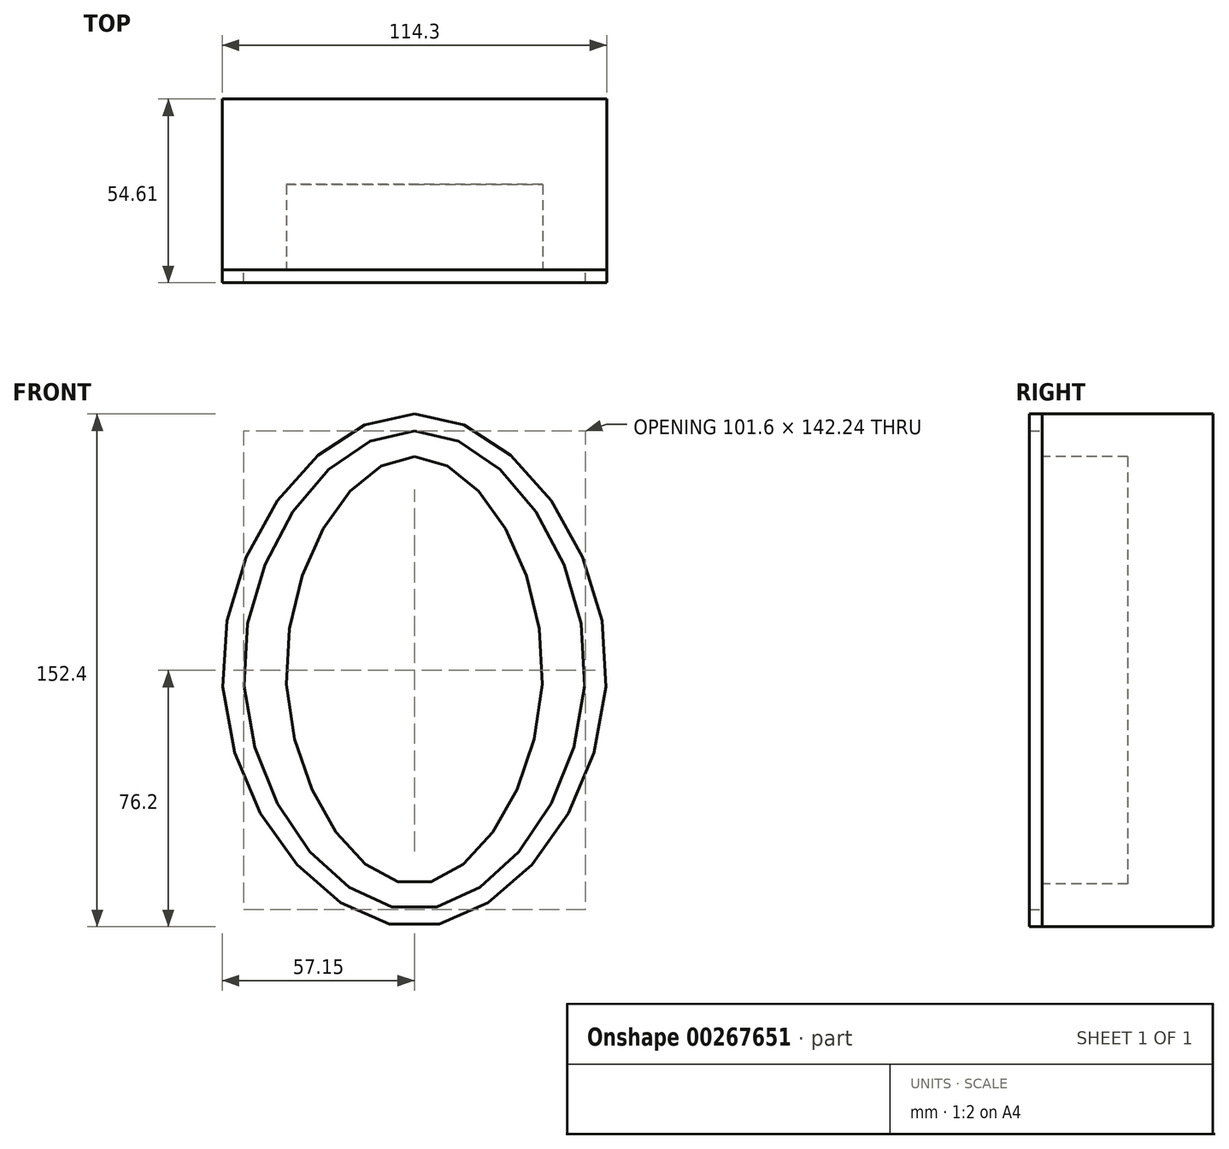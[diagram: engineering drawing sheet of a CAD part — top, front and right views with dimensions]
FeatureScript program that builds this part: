
annotation { "Feature Type Name" : "Feature", "Feature Type Description" : "" }
export const myFeature = defineFeature(function(context is Context, id is Id, definition is map)
    precondition{}
    {
        {
            var Q0;
            Q0=qCreatedBy(makeId("Front.planeOp"),FACE);
            var sketch = newSketch(context, id + "F0", { "sketchPlane" : qUnion([Q0])});
            skFitSpline(sketch, "E0", {"points": [v(0, 76.2) * mm, v(57.15, 0) * mm, v(0, -76.2) * mm, v(-57.15, 0) * mm, v(0, 76.2) * mm]});
            skFitSpline(sketch, "E1", {"points": [v(0, 71.12) * mm, v(50.8, 0) * mm, v(0, -71.12) * mm, v(-50.8, 0) * mm, v(0, 71.12) * mm]});
            skSolve(sketch);
        }
        {
            var Q0;
            Q0=makeQuery(id+"F0.imprint","IMPRINT",FACE,{"disambiguationData":[TD([[makeQuery(id+"F0.imprint","IMPRINT",EDGE,{"derivedFrom":sQuery(id+"F0.wireOp",EDGE,"E0")}),-1.0]])]});
            extrude(context, id + "F1", {"entities" : qUnion([Q0]), "depth" : 3.8 * mm});
        }
        {
            var Q0;
            Q0=makeQuery(id+"F0.imprint","IMPRINT",FACE,{"disambiguationData":[TD([[makeQuery(id+"F0.imprint","IMPRINT",EDGE,{"derivedFrom":sQuery(id+"F0.wireOp",EDGE,"E1")}),-1.0]])]});
            var Q1;
            Q1=makeQuery(id+"F0.imprint","IMPRINT",FACE,{"disambiguationData":[TD([[makeQuery(id+"F0.imprint","IMPRINT",EDGE,{"derivedFrom":sQuery(id+"F0.wireOp",EDGE,"E0")}),-1.0]])]});
            extrude(context, id + "F2", {"entities" : qUnion([Q0, Q1]), "oppositeDirection" : true, "depth" : 50.8 * mm});
        }
        {
            var Q0;
            Q0=makeQuery(id+"F2.opExtrude","CAP_FACE",FACE,{"disambiguationData":[OSD([sQuery(id+"F0.wireOp",EDGE,"E0")])],"isStart":true});
            var sketch = newSketch(context, id + "F3", { "sketchPlane" : qUnion([Q0])});
            skFitSpline(sketch, "E2", {"points": [v(0, 63.5) * mm, v(38.1, 0) * mm, v(0, -63.5) * mm, v(-38.1, 0) * mm, v(0, 63.5) * mm]});
            skSolve(sketch);
        }
        {
            var Q0;
            Q0=makeQuery(id+"F3.imprint","IMPRINT",FACE,{"disambiguationData":[TD([[makeQuery(id+"F3.imprint","IMPRINT",EDGE,{"derivedFrom":sQuery(id+"F3.wireOp",EDGE,"E2")}),-1.0]])]});
            extrude(context, id + "F4", {"entities" : qUnion([Q0]), "operationType" : NewBodyOperationType.REMOVE, "oppositeDirection" : true, "depth" : 25.4 * mm});
        }
    });
